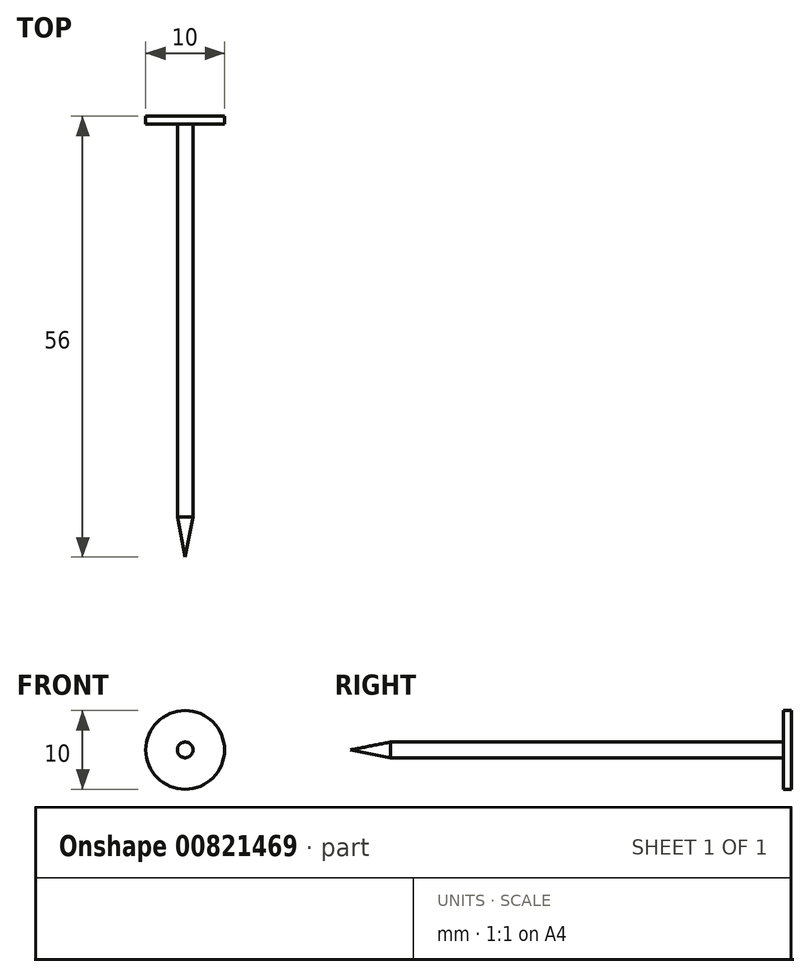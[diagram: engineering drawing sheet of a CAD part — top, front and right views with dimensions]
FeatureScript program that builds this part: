
annotation { "Feature Type Name" : "Feature", "Feature Type Description" : "" }
export const myFeature = defineFeature(function(context is Context, id is Id, definition is map)
    precondition{}
    {
        {
            var Q0;
            Q0=qCreatedBy(makeId("Top.planeOp"),FACE);
            var sketch = newSketch(context, id + "F0", { "sketchPlane" : qUnion([Q0])});
            skLineSegment(sketch, "E0.bottom", {"start": v(-6, 7.04) * mm, "end": v(4, 7.04) * mm});
            skLineSegment(sketch, "E0.top", {"start": v(-6, 6.04) * mm, "end": v(4, 6.04) * mm});
            skLineSegment(sketch, "E0.left", {"start": v(-6, 7.04) * mm, "end": v(-6, 6.04) * mm});
            skLineSegment(sketch, "E0.right", {"start": v(4, 7.04) * mm, "end": v(4, 6.04) * mm});
            skLineSegment(sketch, "E1.bottom", {"start": v(-1, 6.04) * mm, "end": v(0, 6.04) * mm});
            skLineSegment(sketch, "E1.top", {"start": v(-1, -48.96) * mm, "end": v(0, -48.96) * mm});
            skLineSegment(sketch, "E1.left", {"start": v(-1, 6.04) * mm, "end": v(-1, -48.96) * mm});
            skLineSegment(sketch, "E1.right", {"start": v(0, 6.04) * mm, "end": v(0, -48.96) * mm});
            skLineSegment(sketch, "E2", {"start": v(-1, 6.04) * mm, "end": v(-1, 7.85) * mm});
            skSolve(sketch);
        }
        {
            var Q0;
            Q0=makeQuery(id+"F0.imprint","IMPRINT",FACE,{"disambiguationData":[TD([[makeQuery(id+"F0.imprint","IMPRINT",EDGE,{"derivedFrom":sQuery(id+"F0.wireOp",EDGE,"E1.top")}),1.0]])]});
            var Q1;
            {var subQ0=sQuery(id+"F0.wireOp",EDGE,"E0.right");Q1=makeQuery(id+"F0.imprint","IMPRINT",FACE,{"disambiguationData":[TD([[makeQuery(id+"F0.imprint","IMPRINT",EDGE,{"derivedFrom":subQ0}),-1.0]])]});}
            var Q2;
            Q2=sQuery(id+"F0.wireOp",EDGE,"E1.left");
            revolve(context, id + "F1", {"surfaceOperationType" : NewSurfaceOperationType.NEW, "entities" : qUnion([Q0, Q1]), "axis" : qUnion([Q2]), "revolveType" : RevolveType.FULL});
        }
        {
            var Q0;
            Q0=makeQuery(id+"F1.opRevolve","SWEPT_EDGE",EDGE,{"disambiguationData":[OSD([sQuery(id+"F0.wireOp",EDGE,"E1.top"),sQuery(id+"F0.wireOp",EDGE,"E1.right")])]});
            chamfer(context, id + "F2", {"entities" : qUnion([Q0]), "chamferType" : ChamferType.TWO_OFFSETS, "width1" : 5.08 * mm, "oppositeDirection" : false, "width2" : 1 * mm, "tangentPropagation" : true});
        }
    });
